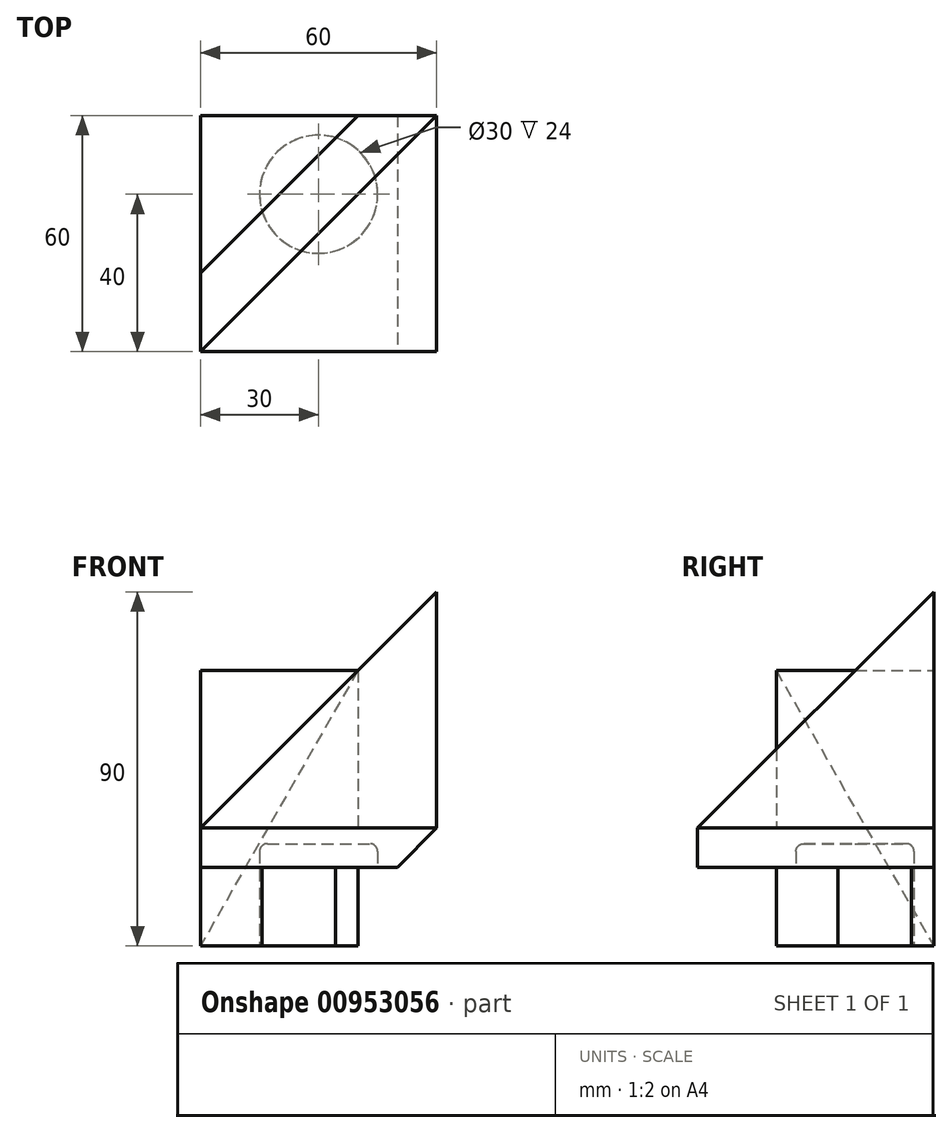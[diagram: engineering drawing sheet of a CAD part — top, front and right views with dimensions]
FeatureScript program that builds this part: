
annotation { "Feature Type Name" : "Feature", "Feature Type Description" : "" }
export const myFeature = defineFeature(function(context is Context, id is Id, definition is map)
    precondition{}
    {
        {
            var Q0;
            Q0=qCreatedBy(makeId("Front.planeOp"),FACE);
            var sketch = newSketch(context, id + "F0", { "sketchPlane" : qUnion([Q0])});
            skLineSegment(sketch, "E0.bottom", {"start": v(0, 0) * mm, "end": v(60, 0) * mm});
            skLineSegment(sketch, "E0.top", {"start": v(0, 10) * mm, "end": v(60, 10) * mm});
            skLineSegment(sketch, "E0.left", {"start": v(0, 0) * mm, "end": v(0, 10) * mm});
            skLineSegment(sketch, "E0.right", {"start": v(60, 0) * mm, "end": v(60, 10) * mm});
            skSolve(sketch);
        }
        {
            var Q0;
            Q0 = qSketchRegion(id + "F0", true);
            extrude(context, id + "F1", {"entities" : qUnion([Q0]), "oppositeDirection" : true, "depth" : 60 * mm, "offsetDistance" : 25 * mm});
        }
        {
            var Q0;
            Q0=makeQuery(id+"F1.opExtrude","SWEPT_EDGE",EDGE,{"disambiguationData":[OSD([sQuery(id+"F0.wireOp",EDGE,"E0.bottom"),sQuery(id+"F0.wireOp",EDGE,"E0.right")])]});
            chamfer(context, id + "F2", {"entities" : qUnion([Q0]), "width" : 10 * mm, "tangentPropagation" : true});
        }
        {
            var Q0;
            Q0=makeQuery(id+"F1.opExtrude","SWEPT_FACE",FACE,{"disambiguationData":[OSD([sQuery(id+"F0.wireOp",EDGE,"E0.top")])]});
            cPlane(context, id + "F3", {"entities" : qUnion([Q0]), "cplaneType" : CPlaneType.OFFSET, "offset" : 60 * mm, "width" : 150 * mm, "height" : 150 * mm});
        }
        {
            var Q0;
            Q0=qCreatedBy(id+"F3.planeOp",FACE);
            var sketch = newSketch(context, id + "F4", { "sketchPlane" : qUnion([Q0])});
            skPoint(sketch, "E1", {"position": v(60, 60) * mm});
            skSolve(sketch);
        }
        {
            var Q0;
            Q0=makeQuery(id+"F1.opExtrude","SWEPT_FACE",FACE,{"disambiguationData":[OSD([sQuery(id+"F0.wireOp",EDGE,"E0.top")])]});
            var sketch = newSketch(context, id + "F5", { "sketchPlane" : qUnion([Q0])});
            skLineSegment(sketch, "E2", {"start": v(60, 60) * mm, "end": v(0, 0) * mm});
            skLineSegment(sketch, "E3", {"start": v(0, 0) * mm, "end": v(60, 0) * mm});
            skLineSegment(sketch, "E4", {"start": v(60, 0) * mm, "end": v(60, 60) * mm});
            skSolve(sketch);
        }
        {
            var Q1;
            Q1=makeQuery(id+"F5.imprint","IMPRINT",FACE,{"disambiguationData":[TD([[makeQuery(id+"F5.imprint","IMPRINT",EDGE,{"derivedFrom":sQuery(id+"F5.wireOp",EDGE,"E2")}),1.0]])]});
            var Q2;
            Q2=sQuery(id+"F4.wireOp",VERTEX,"E1");
            loft(context, id + "F6", {"operationType" : NewBodyOperationType.ADD, "sheetProfilesArray" : [{ "sheetProfileEntities" : qUnion([Q1]) }, { "sheetProfileEntities" : qUnion([Q2]) }]});
        }
        {
            var Q0;
            Q0=makeQuery(id+"F1.opExtrude","SWEPT_FACE",FACE,{"disambiguationData":[OSD([sQuery(id+"F0.wireOp",EDGE,"E0.top")])]});
            var sketch = newSketch(context, id + "F7", { "sketchPlane" : qUnion([Q0])});
            skPoint(sketch, "E5", {"position": v(0, 20) * mm});
            skPoint(sketch, "E6", {"position": v(40, 60) * mm});
            skSolve(sketch);
        }
        {
            var Q0;
            {var subQ1=sQuery(id+"F0.wireOp",EDGE,"E0.top");var subQ3=makeQuery(id+"F1.opExtrude","CAP_EDGE",EDGE,{"disambiguationData":[OSD([subQ1])],"isStart":false});Q0=makeQuery(id+"F7.imprint","IMPRINT",FACE,{"disambiguationData":[TD([[makeQuery(id+"F7.imprint","IMPRINT",EDGE,{"derivedFrom":subQ3}),-1.0]])]});}
            var sketch = newSketch(context, id + "F8", { "sketchPlane" : qUnion([Q0])});
            skLineSegment(sketch, "E7", {"start": v(0, 60) * mm, "end": v(0, 20) * mm});
            skLineSegment(sketch, "E8", {"start": v(0, 20) * mm, "end": v(40, 60) * mm});
            skLineSegment(sketch, "E9", {"start": v(40, 60) * mm, "end": v(0, 60) * mm});
            skSolve(sketch);
        }
        {
            var Q0;
            Q0 = qSketchRegion(id + "F8", true);
            extrude(context, id + "F9", {"entities" : qUnion([Q0]), "operationType" : NewBodyOperationType.ADD, "depth" : 40 * mm, "offsetDistance" : 25 * mm});
        }
        {
            var Q0;
            Q0=makeQuery(id+"F1.opExtrude","SWEPT_FACE",FACE,{"disambiguationData":[OSD([sQuery(id+"F0.wireOp",EDGE,"E0.bottom")])]});
            var sketch = newSketch(context, id + "F10", { "sketchPlane" : qUnion([Q0])});
            skLineSegment(sketch, "E10", {"start": v(0, -60) * mm, "end": v(0, -20) * mm});
            skLineSegment(sketch, "E11", {"start": v(0, -20) * mm, "end": v(40, -60) * mm});
            skLineSegment(sketch, "E12", {"start": v(40, -60) * mm, "end": v(0, -60) * mm});
            skSolve(sketch);
        }
        {
            var Q0;
            Q0 = qSketchRegion(id + "F10", true);
            extrude(context, id + "F11", {"entities" : qUnion([Q0]), "operationType" : NewBodyOperationType.ADD, "depth" : 20 * mm, "offsetDistance" : 25 * mm});
        }
        {
            var Q1;
            Q1=makeQuery(id+"F9.opExtrude","CAP_FACE",FACE,{"disambiguationData":[OSD([sQuery(id+"F8.wireOp",EDGE,"E7"),sQuery(id+"F8.wireOp",EDGE,"E8"),sQuery(id+"F8.wireOp",EDGE,"E9")])],"isStart":false});
            var Q2;
            Q2=makeQuery(id+"F11.opExtrude","CAP_VERTEX",VERTEX,{"disambiguationData":[OSD([sQuery(id+"F10.wireOp",EDGE,"E10"),sQuery(id+"F10.wireOp",EDGE,"E12")])],"isStart":false});
            loft(context, id + "F12", {"operationType" : NewBodyOperationType.REMOVE, "sheetProfilesArray" : [{ "sheetProfileEntities" : qUnion([Q1]) }, { "sheetProfileEntities" : qUnion([Q2]) }]});
        }
        {
            var Q0;
            Q0=makeQuery(id+"F11.opExtrude","CAP_FACE",FACE,{"disambiguationData":[OSD([sQuery(id+"F10.wireOp",EDGE,"E10"),sQuery(id+"F10.wireOp",EDGE,"E11"),sQuery(id+"F10.wireOp",EDGE,"E12")])],"isStart":false});
            var sketch = newSketch(context, id + "F13", { "sketchPlane" : qUnion([Q0])});
            skCircle(sketch, "E13", {"center": v(30, -40) * mm, "radius": 15 * mm});
            skSolve(sketch);
        }
        {
            var Q0;
            Q0 = qSketchRegion(id + "F13", true);
            extrude(context, id + "F14", {"entities" : qUnion([Q0]), "operationType" : NewBodyOperationType.REMOVE, "oppositeDirection" : true, "depth" : 26 * mm, "offsetDistance" : 25 * mm});
        }
        {
            var Q0;
            Q0=makeQuery(id+"F14.boolean.opBoolean","COPY",EDGE,{"derivedFrom":makeQuery(id+"F14.opExtrude","CAP_EDGE",EDGE,{"disambiguationData":[OSD([sQuery(id+"F13.wireOp",EDGE,"E13")])],"isStart":false})});
            fillet(context, id + "F15", {"entities" : qUnion([Q0]), "radius" : 2 * mm, "tangentPropagation" : true, "allowEdgeOverflow" : false});
        }
    });
